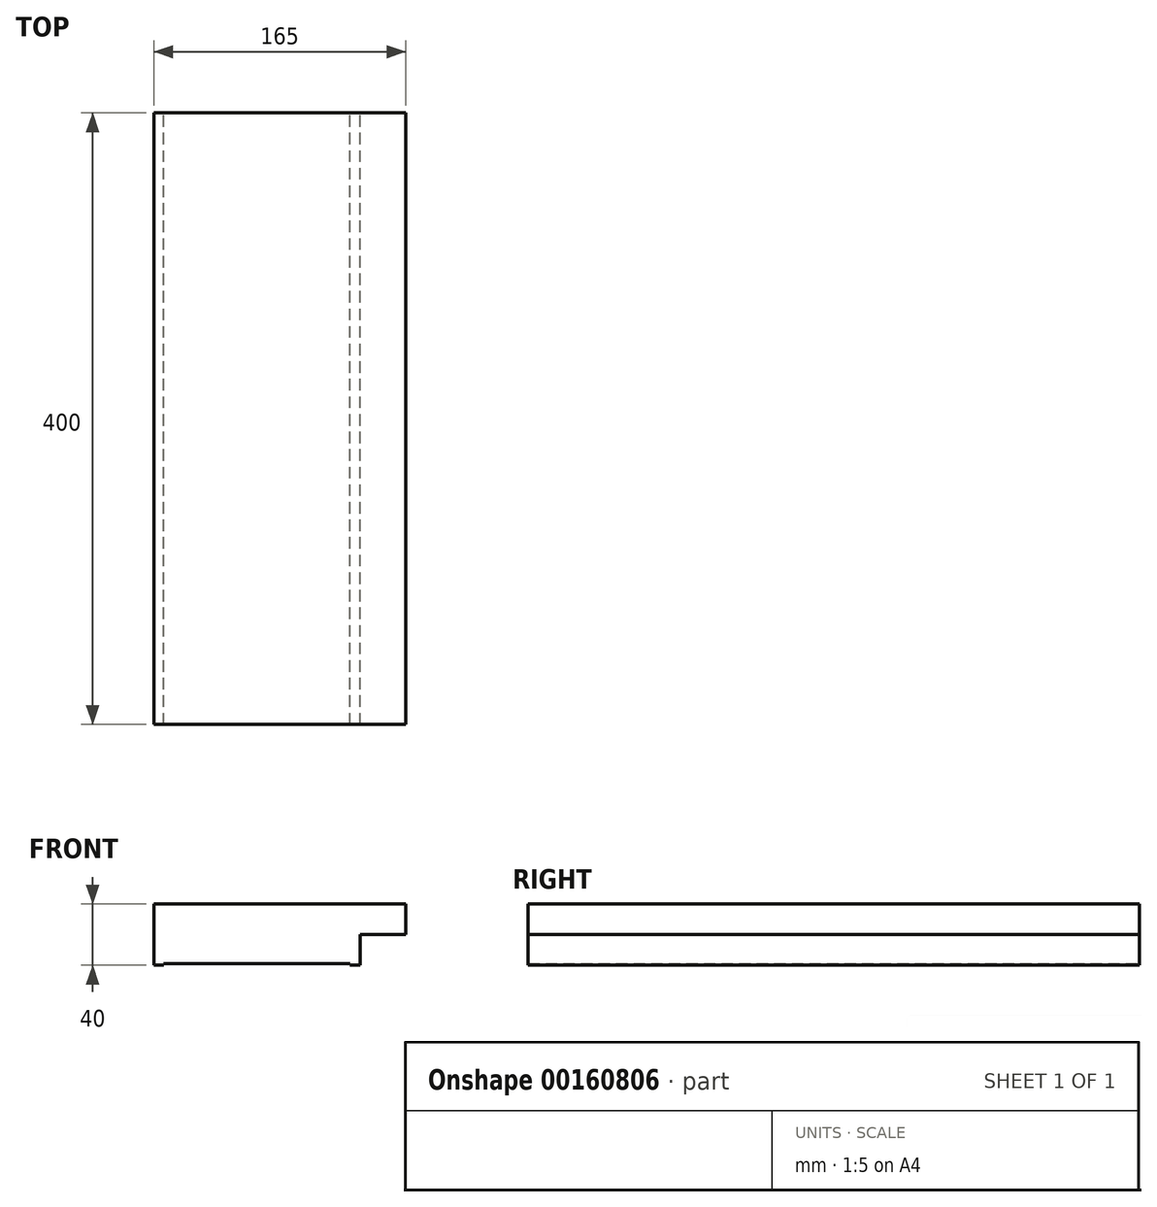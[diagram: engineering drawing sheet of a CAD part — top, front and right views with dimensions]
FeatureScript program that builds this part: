
annotation { "Feature Type Name" : "Feature", "Feature Type Description" : "" }
export const myFeature = defineFeature(function(context is Context, id is Id, definition is map)
    precondition{}
    {
        {
            var Q0;
            Q0=qCreatedBy(makeId("Front.planeOp"),FACE);
            var sketch = newSketch(context, id + "F0", { "sketchPlane" : qUnion([Q0])});
            skLineSegment(sketch, "E0", {"start": v(-54.7, -9.95) * mm, "end": v(-54.7, -49.95) * mm});
            skLineSegment(sketch, "E1", {"start": v(-54.7, -49.95) * mm, "end": v(-48.2, -49.95) * mm});
            skLineSegment(sketch, "E2", {"start": v(-48.2, -49.95) * mm, "end": v(-48.2, -48.95) * mm});
            skLineSegment(sketch, "E3", {"start": v(-48.2, -48.95) * mm, "end": v(73.8, -48.95) * mm});
            skLineSegment(sketch, "E4", {"start": v(73.8, -48.95) * mm, "end": v(73.8, -49.95) * mm});
            skLineSegment(sketch, "E5", {"start": v(73.8, -49.95) * mm, "end": v(80.3, -49.95) * mm});
            skLineSegment(sketch, "E6", {"start": v(80.3, -49.95) * mm, "end": v(80.3, -29.95) * mm});
            skLineSegment(sketch, "E7", {"start": v(80.3, -29.95) * mm, "end": v(110.3, -29.95) * mm});
            skLineSegment(sketch, "E8", {"start": v(110.3, -29.95) * mm, "end": v(110.3, -9.95) * mm});
            skLineSegment(sketch, "E9", {"start": v(110.3, -9.95) * mm, "end": v(-54.7, -9.95) * mm});
            skSolve(sketch);
        }
        {
            var Q0;
            Q0=makeQuery(id+"F0.imprint","IMPRINT",FACE,{"disambiguationData":[TD([[makeQuery(id+"F0.imprint","IMPRINT",EDGE,{"derivedFrom":sQuery(id+"F0.wireOp",EDGE,"E0")}),1.0]])]});
            extrude(context, id + "F1", {"entities" : qUnion([Q0]), "depth" : 400 * mm});
        }
    });
